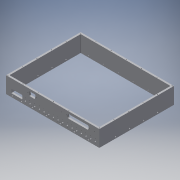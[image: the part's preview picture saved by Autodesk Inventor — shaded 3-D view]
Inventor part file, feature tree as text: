
AUTODESK INVENTOR PART (.ipt)
format: ipt  version: 2017 (Build 210142000, 142)  size: 589,312 bytes
history: native  units: in
note: dims shown in document units (in); Inventor stores cm internally (conversion verified against a paired STEP export)
features: hole x16, other x10, pattern_linear x10, fillet x8, extrude x4, projected_geometry x1, sketch x1
ambient origin geometry x8: Origin, YZ Plane, XZ Plane, XY Plane, X Axis, Y Axis, Z Axis, Center Point
bodies: Solid1 (feature_tree)
feature tree (50):
  extrude  "Extrusion1"  Depth=7.626in
  other  "left-2"
  other  "left-1"
  other  "bottom-1"
  hole  "Hole8"  [1 undecoded]
  hole  "Hole9"  [1 undecoded]
  other  "front-1"
  hole  "Hole10"  [1 undecoded]
  other  "right-1"
  hole  "Hole11"  [1 undecoded]
  hole  "Hole12"  [1 undecoded]
  pattern_linear  "Rectangular Pattern9"  Spacing1=0.0935in  [1 undecoded]
  pattern_linear  "Rectangular Pattern10"  Spacing1=0.0935in  [1 undecoded]
  pattern_linear  "Rectangular Pattern11"  Count1=6 Spacing1=1.562in
  pattern_linear  "Rectangular Pattern12"  Count1=7 Spacing1=1.635in
  hole  "Hole13"  [1 undecoded]
  hole  "Hole16"  [1 undecoded]
  hole  "Hole17"  [1 undecoded]
  extrude  "Extrusion2"  Depth=0.187in
  hole  "Hole18"  [1 undecoded]
  hole  "Hole19"  [1 undecoded]
  hole  "Hole20"  [1 undecoded]
  hole  "Hole21"  [1 undecoded]
  pattern_linear  "Rectangular Pattern13"  Spacing1=1.1693in  [1 undecoded]
  hole  "Hole22"  [1 undecoded]
  pattern_linear  "Rectangular Pattern14"  Spacing1=2.05in  [1 undecoded]
  pattern_linear  "Rectangular Pattern15"  Spacing1=0.41in  [1 undecoded]
  pattern_linear  "Rectangular Pattern16"  Spacing1=0.368in  [1 undecoded]
  pattern_linear  "Rectangular Pattern17"  Spacing1=1.0in  [1 undecoded]
  pattern_linear  "Rectangular Pattern19"  Spacing1=1.75in  [1 undecoded]
  fillet  "Fillet1"  Radius=0.185in
  fillet  "Fillet2"  Radius=1.0in
  fillet  "Fillet3"  Radius=0.185in
  fillet  "Fillet4"  Radius=0.185in
  fillet  "Fillet5"  Radius=1.75in
  fillet  "Fillet6"  Radius=0.185in
  fillet  "Fillet7"  Radius=0.3937in
  fillet  "Fillet8"  Radius=0.562in
  other  "dsub37"
  other  "dsub9"
  hole  "Hole_jackpost_dsub37"  [1 undecoded]
  extrude  "dsub37 cutout"  Depth=0.187in
  hole  "Hole_jackpost_dsub9"  [1 undecoded]
  extrude  "dsub9 cutout"  Depth=0.187in
  hole  "Hole26"  [1 undecoded]
  other  "Ext-Sketch"
  other  "back-1"
  other  "top"
  projected_geometry  "Projected Loop3"
  sketch  "Sketch30"  dims[d6=9.626in d8=7.626in d9=8.0in d10=10.0in d11=0.187in d12=0.187in d13=1.75in d14=0.0in d125=0.0935in d126=0.0935in d127=0.067in d128=0.2in d129=0.375in d130=0.25in d131=0.5635in d132=0.2in d133=0.8108in d134=2.3622in d136=1.562in d137=2.7559in d139=1.635in d140=0.0935in d141=0.0935in d142=0.067in d143=0.2in d144=0.375in d145=0.25in d146=0.5635in d147=0.2in d148=0.8108in d149=2.3622in d151=1.562in d152=2.7559in d154=1.635in d155=0.096in d156=0.75in d157=0.16in d158=0.25in d159=0.5635in d160=1.0in d161=0.8108in d162=0.096in d163=0.75in d164=0.16in d165=0.25in d166=0.5635in d167=1.0in d168=0.8108in d169=0.096in d170=0.75in d171=0.16in d172=0.25in d173=0.5635in d174=1.0in d175=0.8108in d176=0.095in d177=0.095in d180=0.067in d181=0.2in d182=0.375in d183=0.25in d184=0.5635in d185=0.2in d186=0.8108in d197=0.24in d203=0.48in d222=1.1693in d223=0.4094in d224=2.05in d225=0.41in d227=0.368in d238=0.067in d239=0.75in d240=0.375in d241=0.25in d242=0.5635in d243=1.0in d244=0.8108in d245=0.17in d246=0.75in d247=0.375in d248=0.25in d249=0.5635in d250=1.0in d251=0.8108in d252=1.0in d253=0.0in d254=1.75in d255=0.185in d256=1.0in d257=0.185in d259=0.185in d260=1.75in d261=0.185in d262=0.096in d263=0.75in d264=0.16in d265=0.25in d266=0.5635in d267=1.0in d268=0.8108in d271=6.2992in d273=0.5in d274=0.3937in d276=1.0in d278=0.17in d279=0.75in d280=0.375in d281=0.25in d282=0.5635in d283=1.0in d284=0.8108in d285=0.17in d286=0.75in d287=0.375in d288=0.25in d289=0.5635in d290=1.0in d291=0.8108in d292=0.067in d293=0.75in d294=0.375in d295=0.25in d296=0.5635in d297=0.2in d298=0.8108in d299=0.562in d300=2.05in d301=2.05in d302=0.65in d303=0.7874in d305=1.0in d306=0.25in d307=0.185in d308=0.096in d309=0.75in d310=0.16in d311=0.25in d312=0.5635in d313=1.0in d314=0.8108in d315=1.9685in d317=1.5in d318=2.3622in d320=1.6in d321=1.5748in d323=1.5in d324=1.5748in d326=1.5in d331=2.3622in d333=1.562in d334=2.7559in d336=1.635in d338=0.06in d339=0.06in d340=0.06in d341=0.06in d342=0.031in d343=0.031in d344=0.031in d345=0.031in d434=0.17in d477=2.3in d478=0.089in d479=0.089in d482=0.166in d483=0.166in d484=0.57in d485=0.444in d486=0.984in d490=0.23in d491=0.44in d492=0.166in d493=0.166in d496=0.089in d497=1.038in d498=0.089in d499=2.5in d500=0.264in d501=0.264in d502=0.264in d503=0.264in d504=1.983in d505=2.052in d506=0.132in d507=0.132in d508=0.132in d509=0.132in d510=0.21in d511=0.425in d515=0.085in d516=0.224in d517=0.375in d518=0.25in d519=0.5635in d520=0.187in d521=0.8108in d522=1.0in d523=0.0in d524=0.085in d525=0.224in d526=0.375in d527=0.25in d528=0.5635in d529=0.187in d530=0.8108in d531=1.0in d532=0.0in d537=0.085in d538=0.224in d539=0.375in d540=0.25in d541=0.5635in d542=0.187in d543=0.8108in d544=0.47in d545=0.47in d33=1.0in d34=1.0in d383=1.0in d384=1.0in]
note: 24 required parameter values undecoded (feature->parameter linkage not recoverable at this tier; creation-order binding heuristic only, values carry confidence <= 0.55)
